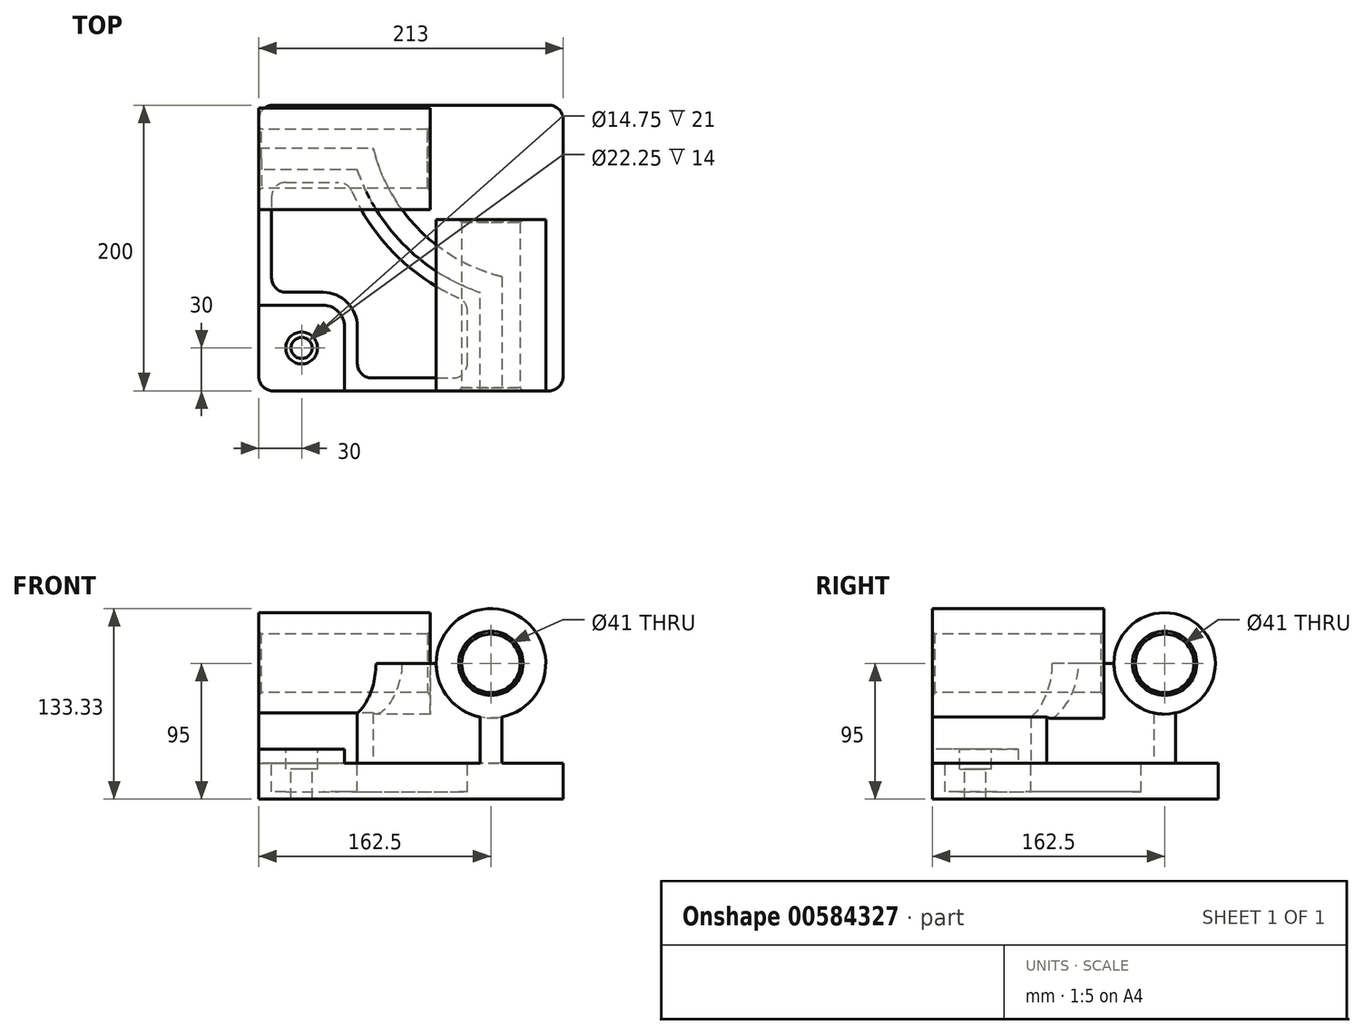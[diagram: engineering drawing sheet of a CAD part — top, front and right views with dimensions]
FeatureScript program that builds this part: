
annotation { "Feature Type Name" : "Feature", "Feature Type Description" : "" }
export const myFeature = defineFeature(function(context is Context, id is Id, definition is map)
    precondition{}
    {
        {
            var Q0;
            Q0=qCreatedBy(makeId("Top.planeOp"),FACE);
            var sketch = newSketch(context, id + "F0", { "sketchPlane" : qUnion([Q0])});
            skLineSegment(sketch, "E0.bottom", {"start": v(106.5, 200) * mm, "end": v(-106.5, 200) * mm});
            skLineSegment(sketch, "E0.top", {"start": v(106.5, 0) * mm, "end": v(-106.5, 0) * mm});
            skLineSegment(sketch, "E0.left", {"start": v(106.5, 200) * mm, "end": v(106.5, 0) * mm});
            skLineSegment(sketch, "E0.right", {"start": v(-106.5, 200) * mm, "end": v(-106.5, 0) * mm});
            skSolve(sketch);
        }
        {
            var Q0;
            Q0 = qSketchRegion(id + "F0", true);
            extrude(context, id + "F1", {"entities" : qUnion([Q0]), "depth" : 25 * mm, "offsetDistance" : 25 * mm});
        }
        {
            var Q0;
            Q0=makeQuery(id+"F1.opExtrude","CAP_FACE",FACE,{"disambiguationData":[OSD([sQuery(id+"F0.wireOp",EDGE,"E0.bottom"),sQuery(id+"F0.wireOp",EDGE,"E0.top"),sQuery(id+"F0.wireOp",EDGE,"E0.left"),sQuery(id+"F0.wireOp",EDGE,"E0.right")])],"isStart":false});
            var sketch = newSketch(context, id + "F2", { "sketchPlane" : qUnion([Q0])});
            skLineSegment(sketch, "E1.0.0", {"start": v(48.5, 0) * mm, "end": v(63.5, 0) * mm});
            skLineSegment(sketch, "E1.0.2", {"start": v(106.5, 200) * mm, "end": v(93.5, 200) * mm});
            skLineSegment(sketch, "E1.0.3", {"start": v(-106.5, 170) * mm, "end": v(-106.5, 155) * mm});
            skLineSegment(sketch, "E2", {"start": v(-106.5, 170) * mm, "end": v(-26.5, 170) * mm});
            skLineSegment(sketch, "E3", {"start": v(-37.69, 155) * mm, "end": v(-106.5, 155) * mm});
            skLineSegment(sketch, "E4", {"start": v(-106.5, 155) * mm, "end": v(-106.5, 170) * mm});
            skLineSegment(sketch, "E5", {"start": v(48.5, 0) * mm, "end": v(48.5, 68.81) * mm});
            skLineSegment(sketch, "E6", {"start": v(63.5, 80) * mm, "end": v(63.5, 0) * mm});
            skLineSegment(sketch, "E7", {"start": v(63.5, 0) * mm, "end": v(48.5, 0) * mm});
            skLineSegment(sketch, "E8", {"start": v(-106.5, 60) * mm, "end": v(-61.5, 60) * mm});
            skLineSegment(sketch, "E9", {"start": v(-46.5, 45) * mm, "end": v(-46.5, 0) * mm});
            skLineSegment(sketch, "E10", {"start": v(-46.5, 0) * mm, "end": v(-106.5, 0) * mm});
            skLineSegment(sketch, "E11", {"start": v(-97.5, 136) * mm, "end": v(-97.5, 79) * mm});
            skLineSegment(sketch, "E12", {"start": v(-87.5, 69) * mm, "end": v(-61.5, 69) * mm});
            skLineSegment(sketch, "E13", {"start": v(-37.5, 45) * mm, "end": v(-37.5, 19) * mm});
            skLineSegment(sketch, "E14", {"start": v(-27.5, 9) * mm, "end": v(29.5, 9) * mm});
            skLineSegment(sketch, "E15", {"start": v(39.5, 19) * mm, "end": v(39.5, 55.88) * mm});
            skLineSegment(sketch, "E16", {"start": v(-87.5, 146) * mm, "end": v(-50.62, 146) * mm});
            skArc(sketch, "E17", {"start": v(-26.5, 170) * mm, "mid": v(6.04, 112.54) * mm, "end": v(63.5, 80) * mm});
            skArc(sketch, "E18", {"start": v(-37.69, 155) * mm, "mid": v(-4.57, 101.93) * mm, "end": v(48.5, 68.81) * mm});
            skArc(sketch, "E19", {"start": v(-41.48, 140.06) * mm, "mid": v(-10.93, 95.57) * mm, "end": v(33.56, 65.02) * mm});
            skLineSegment(sketch, "E20", {"start": v(-106.5, 60) * mm, "end": v(-106.5, 0) * mm});
            skPoint(sketch, "E21.visualSharp", {"position": v(-97.5, 146) * mm});
            skArc(sketch, "E21.filletArc", {"start": v(-87.5, 146) * mm, "mid": v(-94.57, 143.07) * mm, "end": v(-97.5, 136) * mm});
            skPoint(sketch, "E22.visualSharp", {"position": v(-43.97, 146) * mm});
            skArc(sketch, "E22.filletArc", {"start": v(-41.48, 140.06) * mm, "mid": v(-45.17, 144.38) * mm, "end": v(-50.62, 146) * mm});
            skPoint(sketch, "E23.visualSharp", {"position": v(39.5, 62.53) * mm});
            skArc(sketch, "E23.filletArc", {"start": v(39.5, 55.88) * mm, "mid": v(37.88, 61.33) * mm, "end": v(33.56, 65.02) * mm});
            skPoint(sketch, "E24.visualSharp", {"position": v(39.5, 9) * mm});
            skArc(sketch, "E24.filletArc", {"start": v(29.5, 9) * mm, "mid": v(36.57, 11.93) * mm, "end": v(39.5, 19) * mm});
            skPoint(sketch, "E25.visualSharp", {"position": v(-37.5, 9) * mm});
            skArc(sketch, "E25.filletArc", {"start": v(-37.5, 19) * mm, "mid": v(-34.57, 11.93) * mm, "end": v(-27.5, 9) * mm});
            skPoint(sketch, "E26.visualSharp", {"position": v(-97.5, 69) * mm});
            skArc(sketch, "E26.filletArc", {"start": v(-97.5, 79) * mm, "mid": v(-94.57, 71.93) * mm, "end": v(-87.5, 69) * mm});
            skPoint(sketch, "E27.visualSharp", {"position": v(-46.5, 60) * mm});
            skArc(sketch, "E27.filletArc", {"start": v(-46.5, 45) * mm, "mid": v(-50.9, 55.6) * mm, "end": v(-61.5, 60) * mm});
            skPoint(sketch, "E28.visualSharp", {"position": v(-37.5, 69) * mm});
            skArc(sketch, "E28.filletArc", {"start": v(-37.5, 45) * mm, "mid": v(-44.53, 61.97) * mm, "end": v(-61.5, 69) * mm});
            skPoint(sketch, "E29.orphan", {"position": v(-106.5, 200) * mm});
            skPoint(sketch, "E1.0.1.start.orphan", {"position": v(106.5, 0) * mm});
            skSolve(sketch);
        }
        {
            var Q0;
            Q0=makeQuery(id+"F2.imprint","IMPRINT",FACE,{"disambiguationData":[TD([[makeQuery(id+"F2.imprint","IMPRINT",EDGE,{"derivedFrom":sQuery(id+"F2.wireOp",EDGE,"E2")}),-1.0]])]});
            extrude(context, id + "F3", {"entities" : qUnion([Q0]), "operationType" : NewBodyOperationType.ADD, "depth" : 70 * mm, "offsetDistance" : 25 * mm});
        }
        {
            var Q0;
            Q0=makeQuery(id+"F2.imprint","IMPRINT",FACE,{"disambiguationData":[TD([[makeQuery(id+"F2.imprint","IMPRINT",EDGE,{"derivedFrom":sQuery(id+"F2.wireOp",EDGE,"E8")}),-1.0]])]});
            extrude(context, id + "F4", {"entities" : qUnion([Q0]), "operationType" : NewBodyOperationType.ADD, "depth" : 10 * mm, "offsetDistance" : 25 * mm});
        }
        {
            var Q0;
            Q0=makeQuery(id+"F2.imprint","IMPRINT",FACE,{"disambiguationData":[TD([[makeQuery(id+"F2.imprint","IMPRINT",EDGE,{"derivedFrom":sQuery(id+"F2.wireOp",EDGE,"E11")}),1.0]])]});
            extrude(context, id + "F5", {"entities" : qUnion([Q0]), "operationType" : NewBodyOperationType.REMOVE, "oppositeDirection" : true, "depth" : 20 * mm, "offsetDistance" : 25 * mm});
        }
        {
            var Q0;
            Q0=makeQuery(id+"F4.boolean.opBoolean","MERGE",FACE,{"derivedFrom":[makeQuery(id+"F3.boolean.opBoolean","MERGE",FACE,{"derivedFrom":[makeQuery(id+"F1.opExtrude","SWEPT_FACE",FACE,{"disambiguationData":[OSD([sQuery(id+"F0.wireOp",EDGE,"E0.top")])]}),makeQuery(id+"F3.opExtrude","SWEPT_FACE",FACE,{"disambiguationData":[OSD([sQuery(id+"F2.wireOp",EDGE,"E1.0.0")])]})]}),makeQuery(id+"F4.opExtrude","SWEPT_FACE",FACE,{"disambiguationData":[OSD([sQuery(id+"F2.wireOp",EDGE,"E10")])]})]});
            var sketch = newSketch(context, id + "F6", { "sketchPlane" : qUnion([Q0])});
            skCircle(sketch, "E30", {"center": v(56, 95) * mm, "radius": 38.33 * mm});
            skSolve(sketch);
        }
        {
            var Q0;
            Q0 = qSketchRegion(id + "F6", true);
            extrude(context, id + "F7", {"entities" : qUnion([Q0]), "operationType" : NewBodyOperationType.REMOVE, "endBound" : BoundingType.THROUGH_ALL, "oppositeDirection" : true, "depth" : 25 * mm, "offsetDistance" : 25 * mm});
        }
        {
            var Q0;
            Q0=makeQuery(id+"F4.boolean.opBoolean","MERGE",FACE,{"derivedFrom":[makeQuery(id+"F3.boolean.opBoolean","MERGE",FACE,{"derivedFrom":[makeQuery(id+"F1.opExtrude","SWEPT_FACE",FACE,{"disambiguationData":[OSD([sQuery(id+"F0.wireOp",EDGE,"E0.right")])]}),makeQuery(id+"F3.opExtrude","SWEPT_FACE",FACE,{"disambiguationData":[OSD([sQuery(id+"F2.wireOp",EDGE,"E4")])]})]}),makeQuery(id+"F4.opExtrude","SWEPT_FACE",FACE,{"disambiguationData":[OSD([sQuery(id+"F2.wireOp",EDGE,"E20")])]})]});
            var sketch = newSketch(context, id + "F8", { "sketchPlane" : qUnion([Q0])});
            skCircle(sketch, "E31", {"center": v(-162.5, 95) * mm, "radius": 35.5 * mm});
            skSolve(sketch);
        }
        {
            var Q0;
            Q0 = qSketchRegion(id + "F8", true);
            extrude(context, id + "F9", {"entities" : qUnion([Q0]), "operationType" : NewBodyOperationType.REMOVE, "endBound" : BoundingType.THROUGH_ALL, "oppositeDirection" : true, "depth" : 25 * mm, "offsetDistance" : 25 * mm});
        }
        {
            var Q0;
            Q0=makeQuery(id+"F4.boolean.opBoolean","MERGE",FACE,{"derivedFrom":[makeQuery(id+"F3.boolean.opBoolean","MERGE",FACE,{"derivedFrom":[makeQuery(id+"F1.opExtrude","SWEPT_FACE",FACE,{"disambiguationData":[OSD([sQuery(id+"F0.wireOp",EDGE,"E0.top")])]}),makeQuery(id+"F3.opExtrude","SWEPT_FACE",FACE,{"disambiguationData":[OSD([sQuery(id+"F2.wireOp",EDGE,"E1.0.0")])]})]}),makeQuery(id+"F4.opExtrude","SWEPT_FACE",FACE,{"disambiguationData":[OSD([sQuery(id+"F2.wireOp",EDGE,"E10")])]})]});
            var sketch = newSketch(context, id + "F10", { "sketchPlane" : qUnion([Q0])});
            skPoint(sketch, "E32.0", {"position": v(56, 56.67) * mm});
            skCircle(sketch, "E33", {"center": v(56, 95) * mm, "radius": 38.33 * mm});
            skArc(sketch, "E34.0", {"start": v(17.67, 95) * mm, "mid": v(26.36, 70.7) * mm, "end": v(48.5, 57.4) * mm});
            skArc(sketch, "E35.0", {"start": v(48.5, 57.4) * mm, "mid": v(56, 56.67) * mm, "end": v(63.5, 57.4) * mm});
            skCircle(sketch, "E36", {"center": v(56, 95) * mm, "radius": 20.5 * mm});
            skSolve(sketch);
        }
        {
            var Q0;
            Q0 = qSketchRegion(id + "F10", true);
            extrude(context, id + "F11", {"entities" : qUnion([Q0]), "operationType" : NewBodyOperationType.ADD, "oppositeDirection" : true, "depth" : 120 * mm, "offsetDistance" : 25 * mm});
        }
        {
            var Q0;
            Q0=makeQuery(id+"F4.boolean.opBoolean","MERGE",FACE,{"derivedFrom":[makeQuery(id+"F3.boolean.opBoolean","MERGE",FACE,{"derivedFrom":[makeQuery(id+"F1.opExtrude","SWEPT_FACE",FACE,{"disambiguationData":[OSD([sQuery(id+"F0.wireOp",EDGE,"E0.right")])]}),makeQuery(id+"F3.opExtrude","SWEPT_FACE",FACE,{"disambiguationData":[OSD([sQuery(id+"F2.wireOp",EDGE,"E4")])]})]}),makeQuery(id+"F4.opExtrude","SWEPT_FACE",FACE,{"disambiguationData":[OSD([sQuery(id+"F2.wireOp",EDGE,"E20")])]})]});
            var sketch = newSketch(context, id + "F12", { "sketchPlane" : qUnion([Q0])});
            skArc(sketch, "E37.0", {"start": v(-170, 60.3) * mm, "mid": v(-162.5, 59.5) * mm, "end": v(-155, 60.3) * mm});
            skArc(sketch, "E38.0", {"start": v(-155, 60.3) * mm, "mid": v(-134.87, 72.7) * mm, "end": v(-127, 95) * mm});
            skCircle(sketch, "E39", {"center": v(-162.5, 95) * mm, "radius": 35.5 * mm});
            skCircle(sketch, "E40", {"center": v(-162.5, 95) * mm, "radius": 20.5 * mm});
            skSolve(sketch);
        }
        {
            var Q0;
            Q0 = qSketchRegion(id + "F12", true);
            extrude(context, id + "F13", {"entities" : qUnion([Q0]), "operationType" : NewBodyOperationType.ADD, "oppositeDirection" : true, "depth" : 120 * mm, "offsetDistance" : 25 * mm});
        }
        {
            var Q0;
            Q0=makeQuery(id+"F1.opExtrude","SWEPT_EDGE",EDGE,{"disambiguationData":[OSD([sQuery(id+"F0.wireOp",EDGE,"E0.top"),sQuery(id+"F0.wireOp",EDGE,"E0.left")])]});
            var Q1;
            Q1=makeQuery(id+"F1.opExtrude","SWEPT_EDGE",EDGE,{"disambiguationData":[OSD([sQuery(id+"F0.wireOp",EDGE,"E0.bottom"),sQuery(id+"F0.wireOp",EDGE,"E0.left")])]});
            var Q2;
            Q2=makeQuery(id+"F1.opExtrude","SWEPT_EDGE",EDGE,{"disambiguationData":[OSD([sQuery(id+"F0.wireOp",EDGE,"E0.bottom"),sQuery(id+"F0.wireOp",EDGE,"E0.right")])]});
            var Q3;
            Q3=makeQuery(id+"F4.boolean.opBoolean","MERGE",EDGE,{"derivedFrom":[makeQuery(id+"F1.opExtrude","SWEPT_EDGE",EDGE,{"disambiguationData":[OSD([sQuery(id+"F0.wireOp",EDGE,"E0.top"),sQuery(id+"F0.wireOp",EDGE,"E0.right")])]}),makeQuery(id+"F4.opExtrude","SWEPT_EDGE",EDGE,{"disambiguationData":[OSD([sQuery(id+"F2.wireOp",EDGE,"E10"),sQuery(id+"F2.wireOp",EDGE,"E20")])]})]});
            fillet(context, id + "F14", {"entities" : qUnion([Q0, Q1, Q2, Q3]), "radius" : 10 * mm, "tangentPropagation" : true, "allowEdgeOverflow" : false});
        }
        {
            var Q0;
            Q0=makeQuery(id+"F13.opExtrude","CAP_EDGE",EDGE,{"disambiguationData":[OSD([sQuery(id+"F12.wireOp",EDGE,"E40")])],"isStart":true});
            var Q1;
            Q1=makeQuery(id+"F13.opExtrude","CAP_EDGE",EDGE,{"disambiguationData":[OSD([sQuery(id+"F12.wireOp",EDGE,"E40")])],"isStart":false});
            var Q2;
            Q2=makeQuery(id+"F11.opExtrude","CAP_EDGE",EDGE,{"disambiguationData":[OSD([sQuery(id+"F10.wireOp",EDGE,"E36")])],"isStart":false});
            var Q3;
            Q3=makeQuery(id+"F11.opExtrude","CAP_EDGE",EDGE,{"disambiguationData":[OSD([sQuery(id+"F10.wireOp",EDGE,"E36")])],"isStart":true});
            chamfer(context, id + "F15", {"entities" : qUnion([Q0, Q1, Q2, Q3]), "width" : 2 * mm, "tangentPropagation" : true});
        }
        {
            var Q0;
            Q0=makeQuery(id+"F4.opExtrude","CAP_FACE",FACE,{"disambiguationData":[OSD([sQuery(id+"F2.wireOp",EDGE,"E8"),sQuery(id+"F2.wireOp",EDGE,"E9"),sQuery(id+"F2.wireOp",EDGE,"E10"),sQuery(id+"F2.wireOp",EDGE,"E27.filletArc"),sQuery(id+"F2.wireOp",EDGE,"E20")])],"isStart":false});
            var sketch = newSketch(context, id + "F16", { "sketchPlane" : qUnion([Q0])});
            skPoint(sketch, "E41", {"position": v(-76.5, 30) * mm});
            skSolve(sketch);
        }
        {
            var Q0;
            Q0=sQuery(id+"F16.wireOp",VERTEX,"E41");
            var Q1;
            Q1=makeQuery(id+"F1.opExtrude","SWEPT_BODY",BODY,{"disambiguationData":[OSD([sQuery(id+"F0.wireOp",EDGE,"E0.bottom"),sQuery(id+"F0.wireOp",EDGE,"E0.top"),sQuery(id+"F0.wireOp",EDGE,"E0.left"),sQuery(id+"F0.wireOp",EDGE,"E0.right")])]});
            hole(context, id + "F17", {"style" : HoleStyle.C_BORE, "endStyle" : HoleEndStyle.THROUGH, "standardTappedOrClearance" : lookupTablePath({ "standard" : "ISO", "fit" : "Close", "size" : "M14", "type" : "Clearance" }), "standardBlindInLast" : lookupTablePath({ "fit" : "Close", "standard" : "ISO", "size" : "M14", "type" : "Clearance" }), "holeDiameter" : 14.75 * mm, "cBoreDiameter" : 22.25 * mm, "cBoreDepth" : 14 * mm, "majorDiameter" : 5 * mm, "isTappedThrough" : true, "tappedDepth" : 12 * mm, "tapClearance" : 3, "locations" : qUnion([Q0]), "scope" : qUnion([Q1])});
        }
    });
